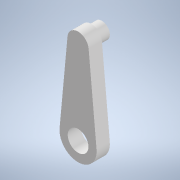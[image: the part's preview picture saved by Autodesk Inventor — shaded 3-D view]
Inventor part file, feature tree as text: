
AUTODESK INVENTOR PART (.ipt)
format: ipt  version: 2022 (Build 260153000, 153)  size: 145,408 bytes
history: native  units: mm
features: reference x8, other x7, extrude x3, sketch x3, projected_geometry x2
ambient origin geometry x8: Origin, YZ Plane, XZ Plane, XY Plane, X Axis, Y Axis, Z Axis, Center Point
bodies: Body1 (feature_tree)
feature tree (23):
  other  "Твердое тело1"
  extrude  "Выдавливание1"  Depth=4.0mm
  extrude  "Выдавливание2"  Depth=3.0mm
  extrude  "Выдавливание3"  Depth=7.0mm
  sketch  "Эскиз1"
  reference  "Ссылка1"
  reference  "Ссылка2"
  reference  "Ссылка3"
  reference  "Ссылка4"
  reference  "Ссылка5"
  sketch  "Эскиз2"
  projected_geometry  "Спроецированная петля1"
  reference  "Ссылка6"
  reference  "Ссылка7"
  reference  "Ссылка8"
  sketch  "Эскиз3"
  projected_geometry  "Спроецированная петля2"
  other  "<userpath>\Documents\Git\MZCAT_2024\MZCAT_2.iam"
  other  "MZCAT_2.iam"
  other  "OCS-D008 B:3"
  other  "lidar_base:1"
  other  "stabilisator_plan:1"
  other  "lidar_krestovina:1"
